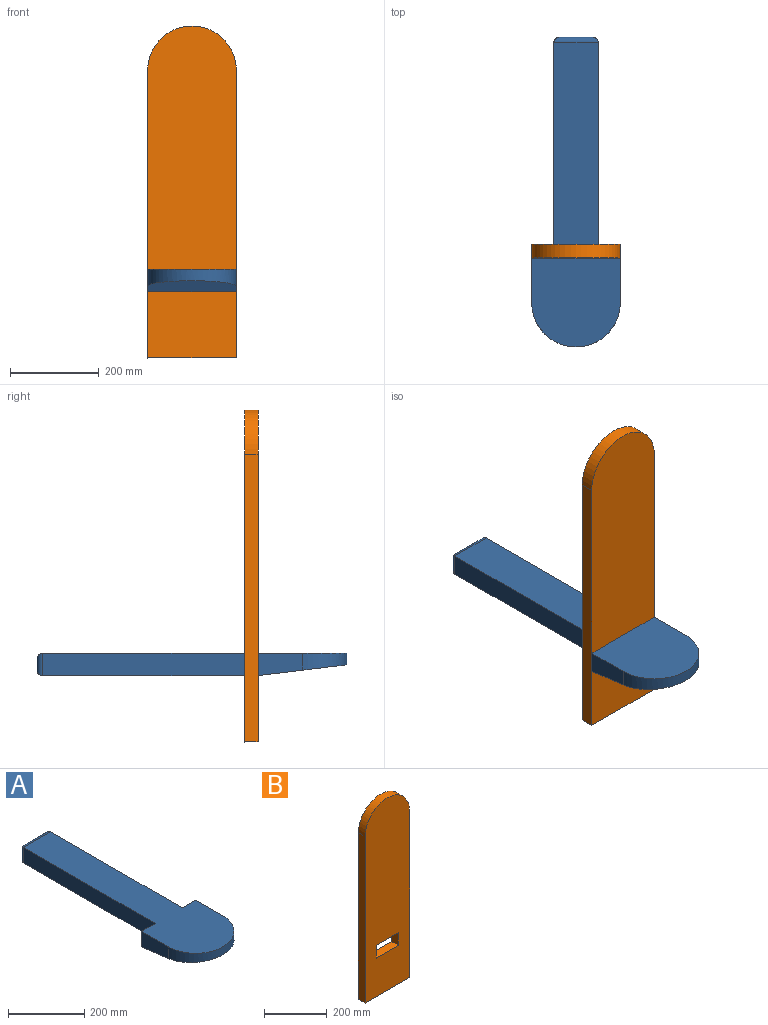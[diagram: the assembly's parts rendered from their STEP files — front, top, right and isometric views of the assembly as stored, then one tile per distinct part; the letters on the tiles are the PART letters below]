
ASSEMBLY  parts=2 mates=1
PART A: 15 faces, bbox 200x700x50 mm
  f0: plane 100x50mm, normal (1,0,0), area 4386.3mm2, adj f3,f6,f8,f10
  f1: plane 100x50mm, normal (-1,0,0), area 4386.3mm2, adj f3,f6,f9,f10
  f2: plane 487.93x100mm, normal (0,0,-1), area 48792.9mm2, adj f4,f7,f10,f14
  f3: cylinder r=100mm len=200mm, axis (0,0,1), area 9396.9mm2, adj f0,f1,f6,f10
  f4: plane 487.93x50mm, normal (1,0,0), area 24396.4mm2, adj f2,f6,f8,f13
  f5: plane 75.86x25.86mm, normal (0,1,0), area 1961.5mm2, adj f11,f12,f13,f14
  f6: plane 687.93x200mm, normal (0,0,1), area 84500.9mm2, adj f0,f1,f3,f4,f7,f8,f9,f11
  f7: plane 487.93x50mm, normal (-1,0,0), area 24396.4mm2, adj f2,f6,f9,f12
  f8: plane 50x50mm, normal (0,1,0), area 2500mm2, adj f0,f4,f6,f10
  f9: plane 50x50mm, normal (0,1,0), area 2500mm2, adj f1,f6,f7,f10
  f10: plane 200x200mm, normal (0,-0.12,-0.99), area 35976mm2, adj f0,f1,f2,f3,f8,f9
  f11: cylinder r=12.07mm len=100mm, axis (-1,0,0), area 1729.8mm2, adj f5,f6,f12,f13
  f12: cylinder r=12.07mm len=50mm, axis (0,0,-1), area 781.7mm2, adj f5,f7,f11,f14
  f13: cylinder r=12.07mm len=50mm, axis (0,0,1), area 781.7mm2, adj f4,f5,f11,f14
  f14: cylinder r=12.07mm len=100mm, axis (1,0,0), area 1729.8mm2, adj f2,f5,f12,f13
PART B: 10 faces, bbox 200x30x750 mm
  f0: plane 650x30mm, normal (-1,0,0), area 19500mm2, adj f1,f3,f4,f5
  f1: plane 200x30mm, normal (0,0,-1), area 6000mm2, adj f0,f2,f4,f5
  f2: plane 650x30mm, normal (1,0,0), area 19500mm2, adj f1,f3,f4,f5
  f3: cylinder r=100mm len=200mm, axis (0,1,0), area 9424.8mm2, adj f0,f2,f4,f5
  f4: plane 750x200mm, normal (0,-1,0), area 140708mm2, adj f0,f1,f2,f3,f6,f7,f8,f9
  f5: plane 750x200mm, normal (0,1,0), area 140708mm2, adj f0,f1,f2,f3,f6,f7,f8,f9
  f6: plane 100x30mm, normal (0,0,1), area 3000mm2, adj f4,f5,f7,f9
  f7: plane 50x30mm, normal (-1,0,0), area 1500mm2, adj f4,f5,f6,f8
  f8: plane 100x30mm, normal (0,0,-1), area 3000mm2, adj f4,f5,f7,f9
  f9: plane 50x30mm, normal (1,0,0), area 1500mm2, adj f4,f5,f6,f8
PLACE A rot(axis=(-0.07,-0.9,0.44),0deg) t=(-40.28,793.03,489.29)mm
PLACE B rot(axis=(-0.07,-0.9,0.44),0deg) t=(-132.08,323.85,437.58)mm
MATE slider B.f5 <-> A.f5  axis (0,1,0) through (-90.28,323.85,547.62)mm
